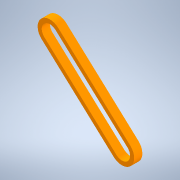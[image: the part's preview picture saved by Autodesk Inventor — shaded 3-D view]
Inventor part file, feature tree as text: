
AUTODESK INVENTOR PART (.ipt)
format: ipt  version: 2022 (Build 260153000, 153)  size: 122,368 bytes
history: native  units: mm
features: other x4, reference x2, extrude x1, sketch x1
ambient origin geometry x8: Origin, YZ Plane, XZ Plane, XY Plane, X Axis, Y Axis, Z Axis, Center Point
bodies: Body1 (feature_tree)
feature tree (8):
  other  "솔리드1"
  extrude  "돌출1"  Depth=0.5mm
  sketch  "스케치2"
  reference  "참조1"
  reference  "참조2"
  other  "조립품1"
  other  "축:1"
  other  "수직축:1"
